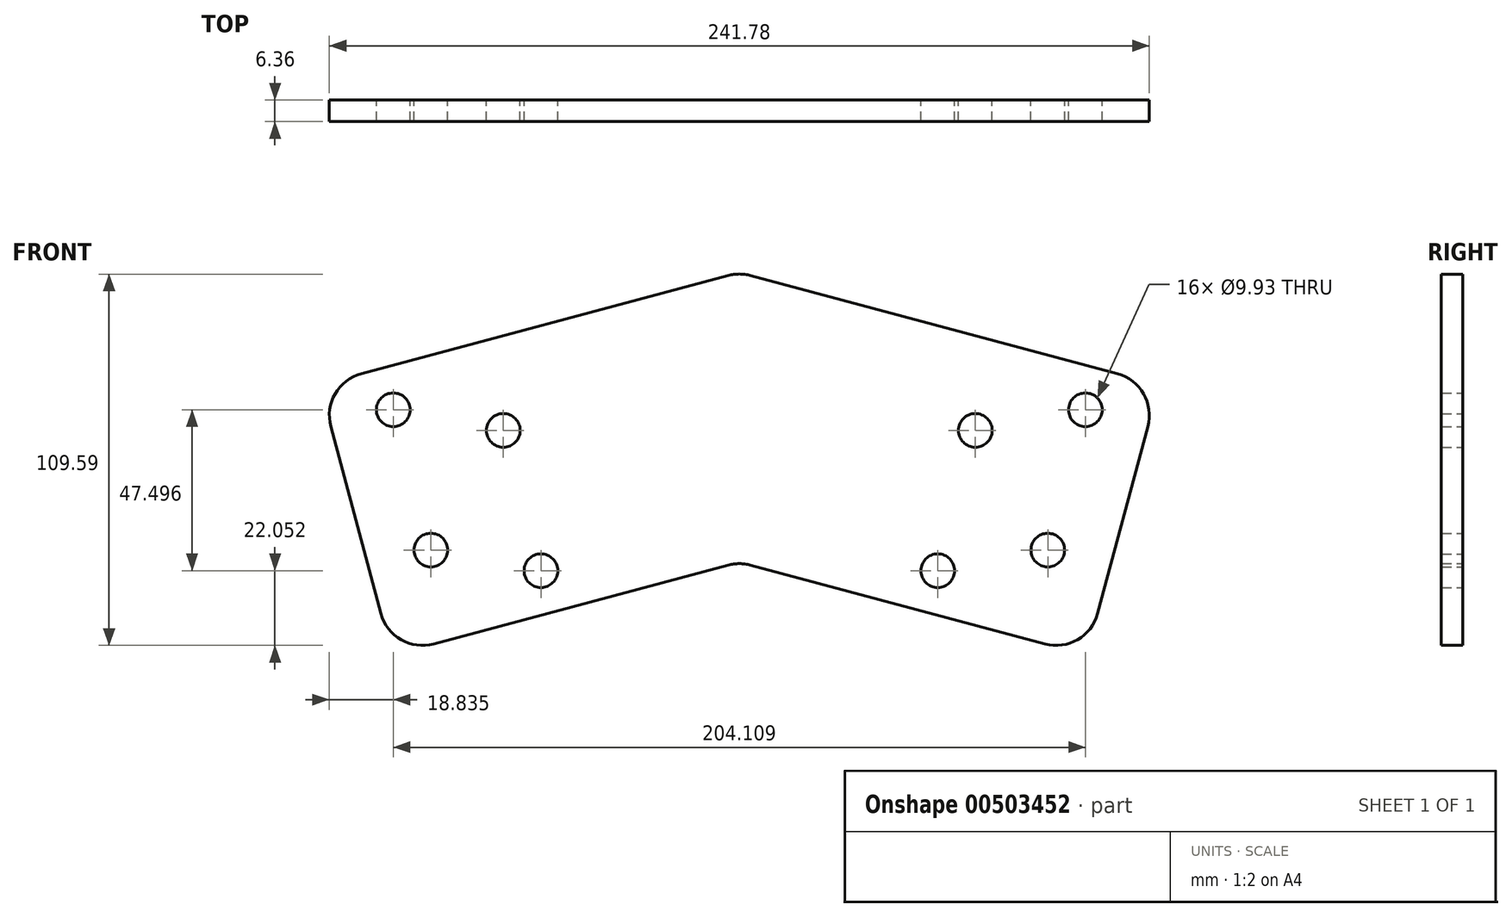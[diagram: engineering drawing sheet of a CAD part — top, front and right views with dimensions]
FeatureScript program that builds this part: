
annotation { "Feature Type Name" : "Feature", "Feature Type Description" : "" }
export const myFeature = defineFeature(function(context is Context, id is Id, definition is map)
    precondition{}
    {
        {
            var Q0;
            Q0=qCreatedBy(makeId("Front.planeOp"),FACE);
            var sketch = newSketch(context, id + "F0", { "sketchPlane" : qUnion([Q0])});
            skLineSegment(sketch, "E0", {"start": v(0, 0) * mm, "end": v(-102.38, -27.43) * mm});
            skLineSegment(sketch, "E1", {"start": v(0, 0) * mm, "end": v(0, 85.46) * mm});
            skLineSegment(sketch, "E2", {"start": v(-102.38, -27.43) * mm, "end": v(-123.74, 52.3) * mm});
            skLineSegment(sketch, "E3", {"start": v(-123.74, 52.3) * mm, "end": v(0, 85.46) * mm});
            skPoint(sketch, "E4", {"position": v(-15.88, 96) * mm});
            skPoint(sketch, "E5", {"position": v(-15.88, -19.05) * mm});
            skLineSegment(sketch, "E6.MirrorCS", {"start": v(0, 0) * mm, "end": v(102.38, -27.43) * mm});
            skPoint(sketch, "E7.MirrorP", {"position": v(15.88, -19.05) * mm});
            skLineSegment(sketch, "E8.MirrorCS", {"start": v(102.38, -27.43) * mm, "end": v(123.74, 52.3) * mm});
            skLineSegment(sketch, "E9.MirrorCS", {"start": v(123.74, 52.3) * mm, "end": v(0, 85.46) * mm});
            skPoint(sketch, "E10.MirrorP", {"position": v(15.88, 96) * mm});
            skLineSegment(sketch, "E11", {"start": v(-15.88, -19.05) * mm, "end": v(-35.6, 54.56) * mm, "construction": true});
            skLineSegment(sketch, "E12", {"start": v(-15.88, 96) * mm, "end": v(3.85, 22.4) * mm, "construction": true});
            skCircle(sketch, "E13", {"center": v(-90.96, 3.57) * mm, "radius": 4.97 * mm});
            skLineSegment(sketch, "E14", {"start": v(-90.96, 3.57) * mm, "end": v(-105.34, 57.24) * mm, "construction": true});
            skCircle(sketch, "E15", {"center": v(-102.05, 44.97) * mm, "radius": 4.97 * mm});
            skCircle(sketch, "E16.MirrorC", {"center": v(90.96, 3.57) * mm, "radius": 4.97 * mm});
            skCircle(sketch, "E17.MirrorC", {"center": v(102.05, 44.97) * mm, "radius": 4.97 * mm});
            skCircle(sketch, "E18", {"center": v(-69.6, 38.87) * mm, "radius": 4.97 * mm});
            skLineSegment(sketch, "E19", {"start": v(-69.6, 38.87) * mm, "end": v(-55.21, -14.8) * mm});
            skCircle(sketch, "E20", {"center": v(-58.5, -2.53) * mm, "radius": 4.97 * mm});
            skCircle(sketch, "E21.MirrorC", {"center": v(58.5, -2.53) * mm, "radius": 4.97 * mm});
            skCircle(sketch, "E22.MirrorC", {"center": v(69.6, 38.87) * mm, "radius": 4.97 * mm});
            skPoint(sketch, "E23", {"position": v(-98.15, 30.4) * mm});
            skSolve(sketch);
        }
        {
            var Q0;
            Q0=qSketchRegion(id+"F0",true);
            extrude(context, id + "F1", {"entities" : qUnion([Q0]), "depth" : 6.35 * mm, "offsetDistance" : 25.4 * mm, "symmetric" : true});
        }
        {
            var Q0;
            Q0=makeQuery(id+"F1.opExtrude","SWEPT_EDGE",EDGE,{"disambiguationData":[OSD([sQuery(id+"F0.wireOp",EDGE,"E2"),sQuery(id+"F0.wireOp",EDGE,"E3")])]});
            var Q1;
            Q1=makeQuery(id+"F1.opExtrude","SWEPT_EDGE",EDGE,{"disambiguationData":[OSD([sQuery(id+"F0.wireOp",EDGE,"E3"),sQuery(id+"F0.wireOp",EDGE,"E1"),sQuery(id+"F0.wireOp",EDGE,"E9.MirrorCS")])]});
            var Q2;
            Q2=makeQuery(id+"F1.opExtrude","SWEPT_EDGE",EDGE,{"disambiguationData":[OSD([sQuery(id+"F0.wireOp",EDGE,"E0"),sQuery(id+"F0.wireOp",EDGE,"E6.MirrorCS"),sQuery(id+"F0.wireOp",EDGE,"E1")])]});
            var Q3;
            Q3=makeQuery(id+"F1.opExtrude","SWEPT_EDGE",EDGE,{"disambiguationData":[OSD([sQuery(id+"F0.wireOp",EDGE,"E6.MirrorCS"),sQuery(id+"F0.wireOp",EDGE,"E8.MirrorCS")])]});
            var Q4;
            Q4=makeQuery(id+"F1.opExtrude","SWEPT_EDGE",EDGE,{"disambiguationData":[OSD([sQuery(id+"F0.wireOp",EDGE,"E8.MirrorCS"),sQuery(id+"F0.wireOp",EDGE,"E9.MirrorCS")])]});
            var Q5;
            Q5=makeQuery(id+"F1.opExtrude","SWEPT_EDGE",EDGE,{"disambiguationData":[OSD([sQuery(id+"F0.wireOp",EDGE,"E0"),sQuery(id+"F0.wireOp",EDGE,"E2")])]});
            fillet(context, id + "F2", {"entities" : qUnion([Q0, Q1, Q2, Q3, Q4, Q5]), "radius" : 12.7 * mm, "tangentPropagation" : true, "allowEdgeOverflow" : false});
        }
    });
